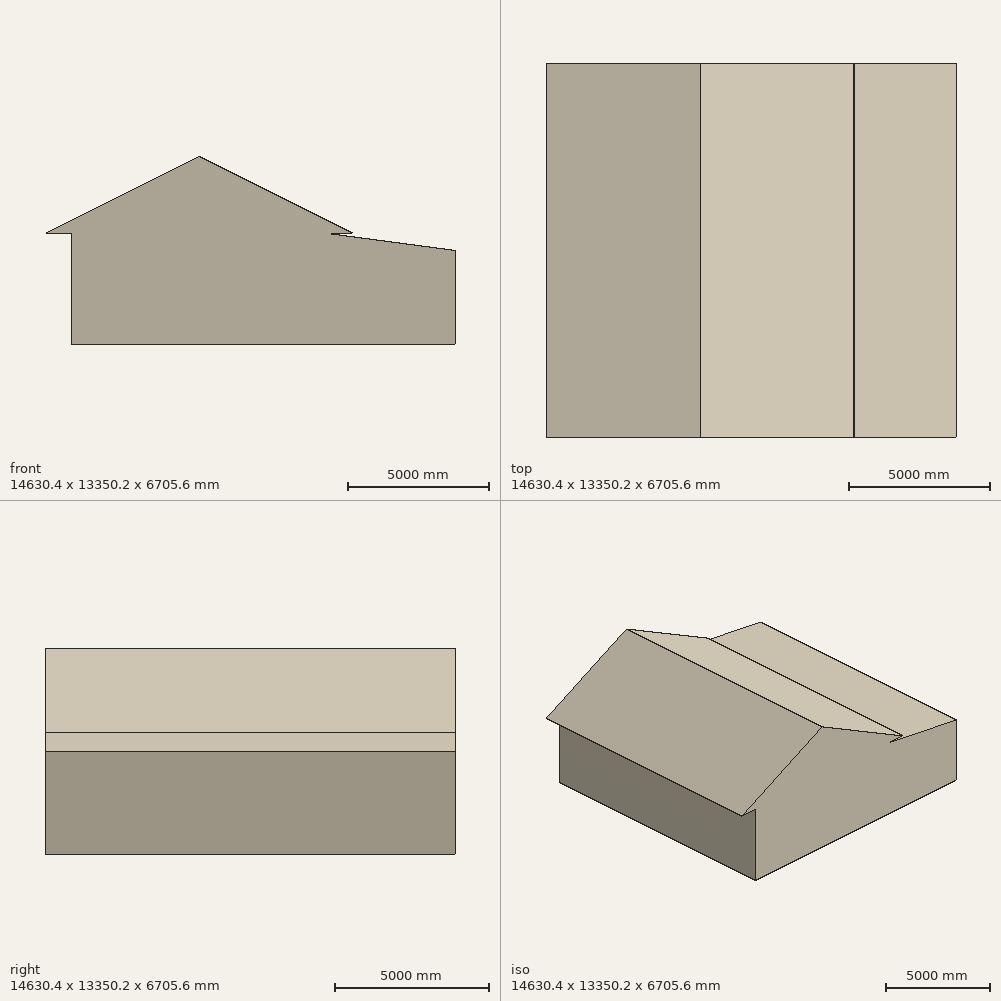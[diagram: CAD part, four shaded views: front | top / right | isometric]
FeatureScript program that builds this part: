
annotation { "Feature Type Name" : "Feature", "Feature Type Description" : "" }
export const myFeature = defineFeature(function(context is Context, id is Id, definition is map)
    precondition{}
    {
        {
            var Q0;
            Q0=qCreatedBy(makeId("Front.planeOp"),FACE);
            var sketch = newSketch(context, id + "F0", { "sketchPlane" : qUnion([Q0])});
            skLineSegment(sketch, "E0", {"start": v(0, 0) * mm, "end": v(-4572, 0) * mm});
            skLineSegment(sketch, "E1", {"start": v(0, 0) * mm, "end": v(4572, 0) * mm});
            skLineSegment(sketch, "E2", {"start": v(0, 0) * mm, "end": v(0, 2286) * mm, "construction": true});
            skLineSegment(sketch, "E3", {"start": v(0, 2286) * mm, "end": v(4572, 0) * mm});
            skLineSegment(sketch, "E4", {"start": v(0, 2286) * mm, "end": v(-4572, 0) * mm});
            skLineSegment(sketch, "E5", {"start": v(-4572, 0) * mm, "end": v(-5486.4, 0) * mm});
            skLineSegment(sketch, "E6", {"start": v(4572, 0) * mm, "end": v(5486.4, 0) * mm});
            skLineSegment(sketch, "E7", {"start": v(0, 2286) * mm, "end": v(0, 2743.2) * mm});
            skLineSegment(sketch, "E8", {"start": v(0, 2743.2) * mm, "end": v(-5486.4, 0) * mm});
            skLineSegment(sketch, "E9", {"start": v(0, 2743.2) * mm, "end": v(5486.4, 0) * mm});
            skLineSegment(sketch, "E10", {"start": v(4572, 0) * mm, "end": v(4572, -3352.8) * mm});
            skLineSegment(sketch, "E11", {"start": v(-4572, 0) * mm, "end": v(-4572, -3352.8) * mm});
            skLineSegment(sketch, "E12", {"start": v(4572, -3352.8) * mm, "end": v(9144, -3352.8) * mm});
            skLineSegment(sketch, "E13", {"start": v(9144, -3352.8) * mm, "end": v(9144, -609.6) * mm});
            skLineSegment(sketch, "E14", {"start": v(9144, -609.6) * mm, "end": v(4572, 0) * mm});
            skLineSegment(sketch, "E15", {"start": v(-4572, -3352.8) * mm, "end": v(4572, -3352.8) * mm});
            skLineSegment(sketch, "E16", {"start": v(-4572, -3352.8) * mm, "end": v(-4572, -3962.4) * mm});
            skLineSegment(sketch, "E17", {"start": v(-4572, -3962.4) * mm, "end": v(9144, -3962.4) * mm});
            skLineSegment(sketch, "E18", {"start": v(9144, -3352.8) * mm, "end": v(9144, -3962.4) * mm});
            skLineSegment(sketch, "E19", {"start": v(9144, -609.6) * mm, "end": v(9144, -1219.2) * mm});
            skLineSegment(sketch, "E20", {"start": v(9144, -1219.2) * mm, "end": v(4572, -609.6) * mm});
            skLineSegment(sketch, "E21", {"start": v(-3352.8, -3352.8) * mm, "end": v(-3352.8, -1219.2) * mm});
            skLineSegment(sketch, "E22", {"start": v(-3352.8, -1219.2) * mm, "end": v(-2438.4, -1219.2) * mm});
            skLineSegment(sketch, "E23", {"start": v(-2438.4, -1219.2) * mm, "end": v(-2438.4, -3352.8) * mm});
            skLineSegment(sketch, "E24", {"start": v(-2438.4, -3352.8) * mm, "end": v(-2117.67, -3352.8) * mm});
            skLineSegment(sketch, "E25.0", {"start": v(-2133.6, -914.4) * mm, "end": v(-2133.6, -3352.8) * mm});
            skLineSegment(sketch, "E25.1", {"start": v(-3657.6, -914.4) * mm, "end": v(-2133.6, -914.4) * mm});
            skLineSegment(sketch, "E25.2", {"start": v(-3657.6, -3352.8) * mm, "end": v(-3657.6, -914.4) * mm});
            skLineSegment(sketch, "E26", {"start": v(3352.8, -2438.4) * mm, "end": v(3352.8, -1066.8) * mm});
            skLineSegment(sketch, "E27", {"start": v(3352.8, -1066.8) * mm, "end": v(609.6, -1066.8) * mm});
            skLineSegment(sketch, "E28", {"start": v(609.6, -1066.8) * mm, "end": v(609.6, -2438.4) * mm});
            skLineSegment(sketch, "E29", {"start": v(609.6, -2438.4) * mm, "end": v(3352.8, -2438.4) * mm});
            skLineSegment(sketch, "E30.0", {"start": v(3505.2, -914.4) * mm, "end": v(457.2, -914.4) * mm});
            skLineSegment(sketch, "E30.1", {"start": v(3505.2, -2590.8) * mm, "end": v(3505.2, -914.4) * mm});
            skLineSegment(sketch, "E30.2", {"start": v(457.2, -2590.8) * mm, "end": v(3505.2, -2590.8) * mm});
            skLineSegment(sketch, "E30.3", {"start": v(457.2, -914.4) * mm, "end": v(457.2, -2590.8) * mm});
            skLineSegment(sketch, "E31.bottom", {"start": v(6096, -1219.2) * mm, "end": v(7315.2, -1219.2) * mm});
            skLineSegment(sketch, "E31.top", {"start": v(6096, -2590.8) * mm, "end": v(7315.2, -2590.8) * mm});
            skLineSegment(sketch, "E31.left", {"start": v(6096, -1219.2) * mm, "end": v(6096, -2590.8) * mm});
            skLineSegment(sketch, "E31.right", {"start": v(7315.2, -1219.2) * mm, "end": v(7315.2, -2590.8) * mm});
            skLineSegment(sketch, "E32", {"start": v(4572, -3352.8) * mm, "end": v(4572, -3962.4) * mm});
            skLineSegment(sketch, "E33.0", {"start": v(5943.6, -1066.8) * mm, "end": v(7467.6, -1066.8) * mm});
            skLineSegment(sketch, "E33.1", {"start": v(5943.6, -1066.8) * mm, "end": v(5943.6, -2743.2) * mm});
            skLineSegment(sketch, "E33.2", {"start": v(5943.6, -2743.2) * mm, "end": v(7467.6, -2743.2) * mm});
            skLineSegment(sketch, "E33.3", {"start": v(7467.6, -1066.8) * mm, "end": v(7467.6, -2743.2) * mm});
            skSolve(sketch);
        }
        {
            var Q0;
            Q0=makeQuery(id+"F0.imprint","IMPRINT",FACE,{"disambiguationData":[TD([[makeQuery(id+"F0.imprint","IMPRINT",EDGE,{"derivedFrom":sQuery(id+"F0.wireOp",EDGE,"E0")}),1.0]])]});
            var Q1;
            Q1=makeQuery(id+"F0.imprint","IMPRINT",FACE,{"disambiguationData":[TD([[makeQuery(id+"F0.imprint","IMPRINT",EDGE,{"derivedFrom":sQuery(id+"F0.wireOp",EDGE,"E26")}),1.0]])]});
            var Q2;
            Q2=makeQuery(id+"F0.imprint","IMPRINT",FACE,{"disambiguationData":[TD([[makeQuery(id+"F0.imprint","IMPRINT",EDGE,{"derivedFrom":sQuery(id+"F0.wireOp",EDGE,"E31.bottom")}),-1.0]])]});
            var Q3;
            Q3=makeQuery(id+"F0.imprint","IMPRINT",FACE,{"disambiguationData":[TD([[makeQuery(id+"F0.imprint","IMPRINT",EDGE,{"derivedFrom":sQuery(id+"F0.wireOp",EDGE,"E3")}),1.0]])]});
            var Q4;
            Q4=makeQuery(id+"F0.imprint","IMPRINT",FACE,{"disambiguationData":[TD([[makeQuery(id+"F0.imprint","IMPRINT",EDGE,{"derivedFrom":sQuery(id+"F0.wireOp",EDGE,"E4")}),-1.0]])]});
            var Q5;
            {var subQ0=sQuery(id+"F0.wireOp",EDGE,"E14");Q5=makeQuery(id+"F0.imprint","IMPRINT",FACE,{"disambiguationData":[TD([[makeQuery(id+"F0.imprint","IMPRINT",EDGE,{"derivedFrom":subQ0}),1.0]])]});}
            var Q6;
            Q6=makeQuery(id+"F0.imprint","IMPRINT",FACE,{"disambiguationData":[TD([[makeQuery(id+"F0.imprint","IMPRINT",EDGE,{"derivedFrom":sQuery(id+"F0.wireOp",EDGE,"E12")}),-1.0]])]});
            var Q7;
            {var subQ0=sQuery(id+"F0.wireOp",EDGE,"E21");Q7=makeQuery(id+"F0.imprint","IMPRINT",FACE,{"disambiguationData":[TD([[makeQuery(id+"F0.imprint","IMPRINT",EDGE,{"derivedFrom":subQ0}),-1.0]])]});}
            var Q8;
            Q8=makeQuery(id+"F0.imprint","IMPRINT",FACE,{"disambiguationData":[TD([[makeQuery(id+"F0.imprint","IMPRINT",EDGE,{"derivedFrom":sQuery(id+"F0.wireOp",EDGE,"E26")}),-1.0]])]});
            var Q9;
            Q9=makeQuery(id+"F0.imprint","IMPRINT",FACE,{"disambiguationData":[TD([[makeQuery(id+"F0.imprint","IMPRINT",EDGE,{"derivedFrom":sQuery(id+"F0.wireOp",EDGE,"E31.bottom")}),1.0]])]});
            var Q10;
            Q10=makeQuery(id+"F0.imprint","IMPRINT",FACE,{"disambiguationData":[TD([[makeQuery(id+"F0.imprint","IMPRINT",EDGE,{"derivedFrom":sQuery(id+"F0.wireOp",EDGE,"E0")}),-1.0]])]});
            var Q11;
            {var subQ1=sQuery(id+"F0.wireOp",EDGE,"E21");Q11=makeQuery(id+"F0.imprint","IMPRINT",FACE,{"disambiguationData":[TD([[makeQuery(id+"F0.imprint","IMPRINT",EDGE,{"derivedFrom":subQ1}),1.0]])]});}
            var Q12;
            {var subQ1=sQuery(id+"F0.wireOp",EDGE,"E12");Q12=makeQuery(id+"F0.imprint","IMPRINT",FACE,{"disambiguationData":[TD([[makeQuery(id+"F0.imprint","IMPRINT",EDGE,{"derivedFrom":subQ1}),1.0]])]});}
            var Q13;
            {var subQ8=sQuery(id+"F0.wireOp",EDGE,"E16");Q13=makeQuery(id+"F0.imprint","IMPRINT",FACE,{"disambiguationData":[TD([[makeQuery(id+"F0.imprint","IMPRINT",EDGE,{"derivedFrom":subQ8}),1.0]])]});}
            extrude(context, id + "F1", {"entities" : qUnion([Q0, Q1, Q2, Q3, Q4, Q5, Q6, Q7, Q8, Q9, Q10, Q11, Q12, Q13]), "depth" : 13350.24 * mm, "offsetDistance" : 30.48 * mm});
        }
        {
            var Q0;
            {var subQ1=sQuery(id+"F0.wireOp",EDGE,"E21");Q0=makeQuery(id+"F0.imprint","IMPRINT",FACE,{"disambiguationData":[TD([[makeQuery(id+"F0.imprint","IMPRINT",EDGE,{"derivedFrom":subQ1}),1.0]])]});}
            var Q1;
            {var subQ0=sQuery(id+"F0.wireOp",EDGE,"E21");Q1=makeQuery(id+"F0.imprint","IMPRINT",FACE,{"disambiguationData":[TD([[makeQuery(id+"F0.imprint","IMPRINT",EDGE,{"derivedFrom":subQ0}),-1.0]])]});}
            extrude(context, id + "F2", {"entities" : qUnion([Q0, Q1]), "operationType" : NewBodyOperationType.ADD, "depth" : 30.48 * mm, "offsetDistance" : 30.48 * mm});
        }
        {
            var Q0;
            Q0=makeQuery(id+"F0.imprint","IMPRINT",FACE,{"disambiguationData":[TD([[makeQuery(id+"F0.imprint","IMPRINT",EDGE,{"derivedFrom":sQuery(id+"F0.wireOp",EDGE,"E4")}),-1.0]])]});
            var Q1;
            Q1=makeQuery(id+"F0.imprint","IMPRINT",FACE,{"disambiguationData":[TD([[makeQuery(id+"F0.imprint","IMPRINT",EDGE,{"derivedFrom":sQuery(id+"F0.wireOp",EDGE,"E3")}),1.0]])]});
            var Q2;
            {var subQ0=sQuery(id+"F0.wireOp",EDGE,"E14");Q2=makeQuery(id+"F0.imprint","IMPRINT",FACE,{"disambiguationData":[TD([[makeQuery(id+"F0.imprint","IMPRINT",EDGE,{"derivedFrom":subQ0}),1.0]])]});}
            var Q3;
            Q3=makeQuery(id+"F0.imprint","IMPRINT",FACE,{"disambiguationData":[TD([[makeQuery(id+"F0.imprint","IMPRINT",EDGE,{"derivedFrom":sQuery(id+"F0.wireOp",EDGE,"E12")}),-1.0]])]});
            var Q4;
            {var subQ8=sQuery(id+"F0.wireOp",EDGE,"E16");Q4=makeQuery(id+"F0.imprint","IMPRINT",FACE,{"disambiguationData":[TD([[makeQuery(id+"F0.imprint","IMPRINT",EDGE,{"derivedFrom":subQ8}),1.0]])]});}
            extrude(context, id + "F3", {"entities" : qUnion([Q0, Q1, Q2, Q3, Q4]), "operationType" : NewBodyOperationType.ADD, "depth" : 9144 * mm, "offsetDistance" : 30.48 * mm});
        }
    });
